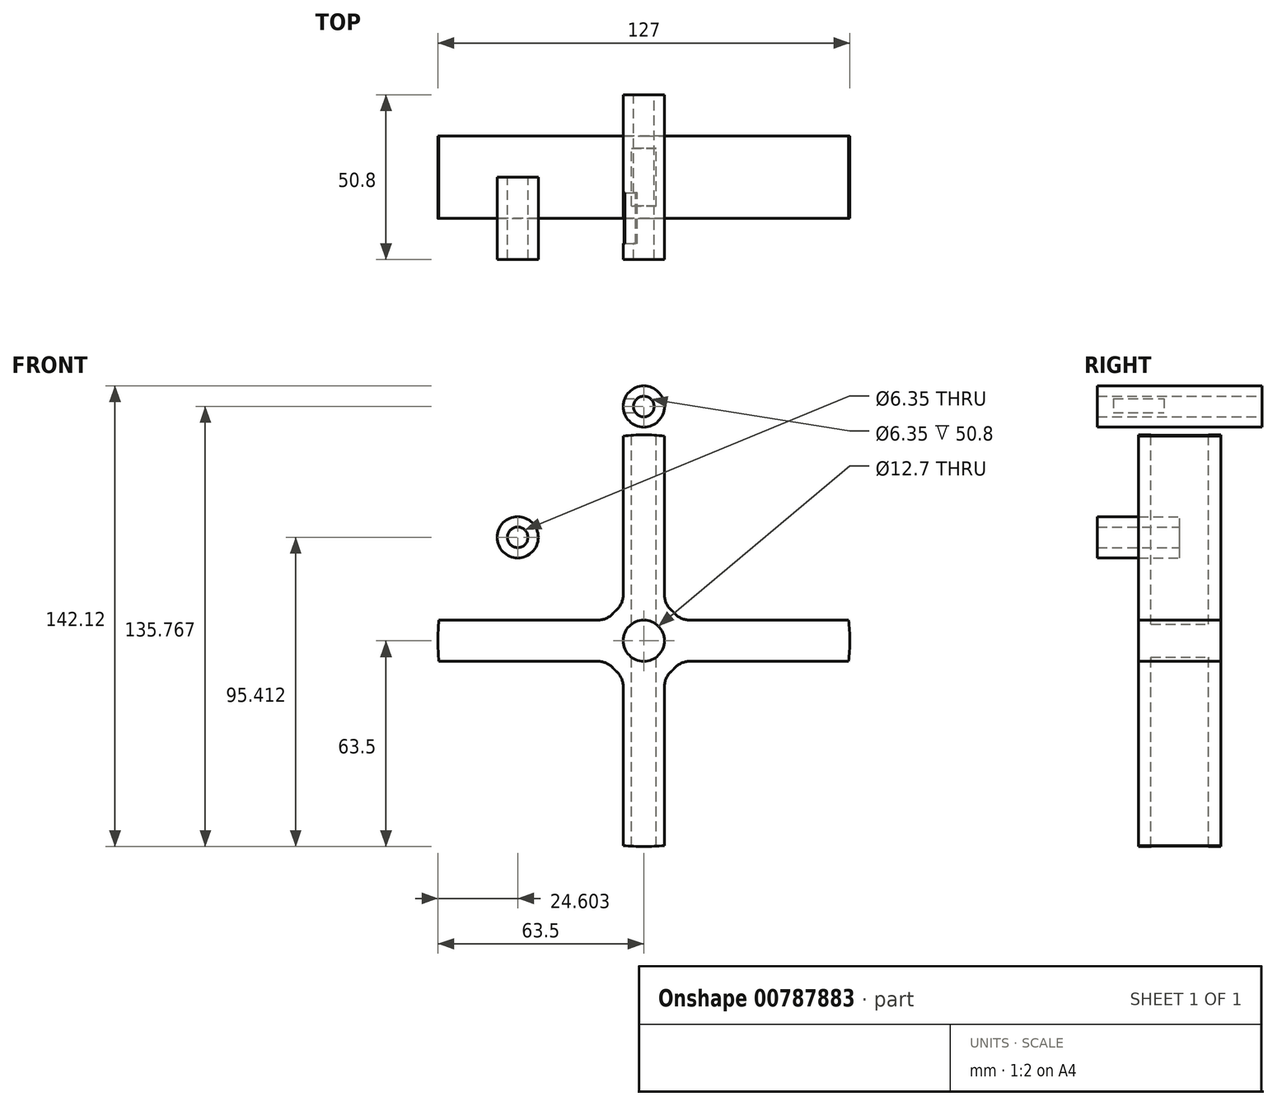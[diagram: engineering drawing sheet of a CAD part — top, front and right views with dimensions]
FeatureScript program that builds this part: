
annotation { "Feature Type Name" : "Feature", "Feature Type Description" : "" }
export const myFeature = defineFeature(function(context is Context, id is Id, definition is map)
    precondition{}
    {
        {
            var Q0;
            Q0=qCreatedBy(makeId("Front.planeOp"),FACE);
            var sketch = newSketch(context, id + "F0", { "sketchPlane" : qUnion([Q0])});
            skArc(sketch, "E0", {"start": v(6.35, 63.18) * mm, "mid": v(0, 63.5) * mm, "end": v(-6.35, 63.18) * mm});
            skArc(sketch, "E1", {"start": v(-8.47, 9.47) * mm, "mid": v(-8.98, 8.98) * mm, "end": v(-9.47, 8.47) * mm});
            skLineSegment(sketch, "E2", {"start": v(-6.35, 63.18) * mm, "end": v(-6.35, 14.2) * mm});
            skLineSegment(sketch, "E3", {"start": v(-63.18, 6.35) * mm, "end": v(-14.2, 6.35) * mm});
            skLineSegment(sketch, "E4", {"start": v(63.18, -6.35) * mm, "end": v(14.2, -6.35) * mm});
            skLineSegment(sketch, "E5", {"start": v(6.35, 63.18) * mm, "end": v(6.35, 14.2) * mm});
            skPoint(sketch, "E6.orphan", {"position": v(76.76, 6.35) * mm});
            skPoint(sketch, "E7.orphan", {"position": v(76.76, -6.35) * mm});
            skLineSegment(sketch, "E8.trimOffspring", {"start": v(-6.35, -14.2) * mm, "end": v(-6.35, -63.18) * mm});
            skLineSegment(sketch, "E9.trimOffspring", {"start": v(14.2, 6.35) * mm, "end": v(63.18, 6.35) * mm});
            skLineSegment(sketch, "E10.trimOffspring", {"start": v(-14.2, -6.35) * mm, "end": v(-63.18, -6.35) * mm});
            skLineSegment(sketch, "E11.trimOffspring", {"start": v(6.35, -14.2) * mm, "end": v(6.35, -63.18) * mm});
            skArc(sketch, "E12.trimOffspring", {"start": v(-63.18, 6.35) * mm, "mid": v(-63.5, 0) * mm, "end": v(-63.18, -6.35) * mm});
            skArc(sketch, "E13.trimOffspring", {"start": v(-6.35, -63.18) * mm, "mid": v(0, -63.5) * mm, "end": v(6.35, -63.18) * mm});
            skArc(sketch, "E14.trimOffspring", {"start": v(63.18, -6.35) * mm, "mid": v(63.5, 0) * mm, "end": v(63.18, 6.35) * mm});
            skCircle(sketch, "E15", {"center": v(0, 0) * mm, "radius": 6.35 * mm});
            skArc(sketch, "E16.trimOffspring", {"start": v(-9.47, -8.47) * mm, "mid": v(-8.98, -8.98) * mm, "end": v(-8.47, -9.47) * mm});
            skArc(sketch, "E17.trimOffspring", {"start": v(8.47, -9.47) * mm, "mid": v(8.98, -8.98) * mm, "end": v(9.47, -8.47) * mm});
            skArc(sketch, "E18.trimOffspring", {"start": v(9.47, 8.47) * mm, "mid": v(8.98, 8.98) * mm, "end": v(8.47, 9.47) * mm});
            skPoint(sketch, "E19.visualSharp", {"position": v(-6.35, 11) * mm});
            skArc(sketch, "E19.filletArc", {"start": v(-8.47, 9.47) * mm, "mid": v(-6.9, 11.6) * mm, "end": v(-6.35, 14.2) * mm});
            skPoint(sketch, "E20.visualSharp", {"position": v(-11, 6.35) * mm});
            skArc(sketch, "E20.filletArc", {"start": v(-14.2, 6.35) * mm, "mid": v(-11.6, 6.9) * mm, "end": v(-9.47, 8.47) * mm});
            skPoint(sketch, "E21.visualSharp", {"position": v(6.35, 11) * mm});
            skArc(sketch, "E21.filletArc", {"start": v(6.35, 14.2) * mm, "mid": v(6.9, 11.6) * mm, "end": v(8.47, 9.47) * mm});
            skPoint(sketch, "E22.visualSharp", {"position": v(11, 6.35) * mm});
            skArc(sketch, "E22.filletArc", {"start": v(9.47, 8.47) * mm, "mid": v(11.6, 6.9) * mm, "end": v(14.2, 6.35) * mm});
            skPoint(sketch, "E23.visualSharp", {"position": v(11, -6.35) * mm});
            skArc(sketch, "E23.filletArc", {"start": v(14.2, -6.35) * mm, "mid": v(11.6, -6.9) * mm, "end": v(9.47, -8.47) * mm});
            skPoint(sketch, "E24.visualSharp", {"position": v(6.35, -11) * mm});
            skArc(sketch, "E24.filletArc", {"start": v(8.47, -9.47) * mm, "mid": v(6.9, -11.6) * mm, "end": v(6.35, -14.2) * mm});
            skPoint(sketch, "E25.visualSharp", {"position": v(-6.35, -11) * mm});
            skArc(sketch, "E25.filletArc", {"start": v(-6.35, -14.2) * mm, "mid": v(-6.9, -11.6) * mm, "end": v(-8.47, -9.47) * mm});
            skPoint(sketch, "E26.visualSharp", {"position": v(-11, -6.35) * mm});
            skArc(sketch, "E26.filletArc", {"start": v(-9.47, -8.47) * mm, "mid": v(-11.6, -6.9) * mm, "end": v(-14.2, -6.35) * mm});
            skSolve(sketch);
        }
        {
            var Q0;
            Q0 = qSketchRegion(id + "F0", true);
            extrude(context, id + "F1", {"entities" : qUnion([Q0]), "depth" : 25.4 * mm, "offsetDistance" : 25.4 * mm, "symmetric" : true});
        }
        {
            var Q0;
            Q0=qCreatedBy(makeId("Top.planeOp"),FACE);
            var sketch = newSketch(context, id + "F2", { "sketchPlane" : qUnion([Q0])});
            skLineSegment(sketch, "E27", {"start": v(-3.81, 8.9) * mm, "end": v(-3.8, -8.9) * mm});
            skLineSegment(sketch, "E28", {"start": v(3.8, 8.9) * mm, "end": v(3.81, -8.9) * mm});
            skLineSegment(sketch, "E29", {"start": v(3.81, -8.9) * mm, "end": v(-3.8, -8.9) * mm});
            skLineSegment(sketch, "E30", {"start": v(3.8, 8.9) * mm, "end": v(-3.81, 8.9) * mm});
            skPoint(sketch, "E31.orphan", {"position": v(3.81, -31.13) * mm});
            skPoint(sketch, "E32.orphan", {"position": v(-3.8, -31.13) * mm});
            skSolve(sketch);
        }
        {
            var Q0;
            Q0 = qSketchRegion(id + "F2", true);
            extrude(context, id + "F3", {"entities" : qUnion([Q0]), "operationType" : NewBodyOperationType.REMOVE, "oppositeDirection" : true, "depth" : 127 * mm, "offsetDistance" : 25.4 * mm, "symmetric" : true});
        }
        {
            var Q0;
            Q0=qCreatedBy(makeId("Front.planeOp"),FACE);
            var sketch = newSketch(context, id + "F4", { "sketchPlane" : qUnion([Q0])});
            skCircle(sketch, "E33", {"center": v(0, 72.27) * mm, "radius": 6.35 * mm});
            skCircle(sketch, "E34", {"center": v(0, -71.12) * mm, "radius": 6.35 * mm});
            skCircle(sketch, "E35", {"center": v(0, 72.27) * mm, "radius": 3.18 * mm});
            skSolve(sketch);
        }
        {
            var Q0;
            Q0=makeQuery(id+"F4.imprint","IMPRINT",FACE,{"disambiguationData":[TD([[makeQuery(id+"F4.imprint","IMPRINT",EDGE,{"derivedFrom":sQuery(id+"F4.wireOp",EDGE,"E33")}),1.0]])]});
            extrude(context, id + "F5", {"entities" : qUnion([Q0]), "depth" : 50.8 * mm, "offsetDistance" : 25.4 * mm, "symmetric" : true});
        }
        {
            var Q0;
            Q0=qCreatedBy(makeId("Right.planeOp"),FACE);
            var sketch = newSketch(context, id + "F6", { "sketchPlane" : qUnion([Q0])});
            skLineSegment(sketch, "E36.bottom", {"start": v(-4.87, 74.72) * mm, "end": v(-20.47, 74.72) * mm});
            skLineSegment(sketch, "E36.top", {"start": v(-4.87, 70.35) * mm, "end": v(-20.47, 70.35) * mm});
            skLineSegment(sketch, "E36.left", {"start": v(-4.87, 74.72) * mm, "end": v(-4.87, 70.35) * mm});
            skLineSegment(sketch, "E36.right", {"start": v(-20.47, 74.72) * mm, "end": v(-20.47, 70.35) * mm});
            skSolve(sketch);
        }
        {
            var Q0;
            Q0=makeQuery(id+"F6.imprint","IMPRINT",FACE,{"disambiguationData":[TD([[makeQuery(id+"F6.imprint","IMPRINT",EDGE,{"derivedFrom":sQuery(id+"F6.wireOp",EDGE,"E36.bottom")}),1.0]])]});
            extrude(context, id + "F7", {"entities" : qUnion([Q0]), "operationType" : NewBodyOperationType.REMOVE, "oppositeDirection" : true, "depth" : 7.62 * mm, "offsetDistance" : 25.4 * mm});
        }
        {
            var Q0;
            Q0=qCreatedBy(makeId("Front.planeOp"),FACE);
            var sketch = newSketch(context, id + "F8", { "sketchPlane" : qUnion([Q0])});
            skCircle(sketch, "E37", {"center": v(-38.9, 31.91) * mm, "radius": 6.35 * mm});
            skCircle(sketch, "E38", {"center": v(-38.9, 31.91) * mm, "radius": 3.18 * mm});
            skSolve(sketch);
        }
        {
            var Q0;
            Q0=makeQuery(id+"F8.imprint","IMPRINT",FACE,{"disambiguationData":[TD([[makeQuery(id+"F8.imprint","IMPRINT",EDGE,{"derivedFrom":sQuery(id+"F8.wireOp",EDGE,"E37")}),1.0]])]});
            var Q1;
            Q1=sQuery(id+"F8.wireOp",EDGE,"E37");
            var Q2;
            Q2=sQuery(id+"F8.wireOp",EDGE,"E38");
            extrude(context, id + "F9", {"entities" : qUnion([Q0]), "surfaceEntities" : qUnion([Q1, Q2]), "depth" : 25.4 * mm, "offsetDistance" : 25.4 * mm});
        }
    });
